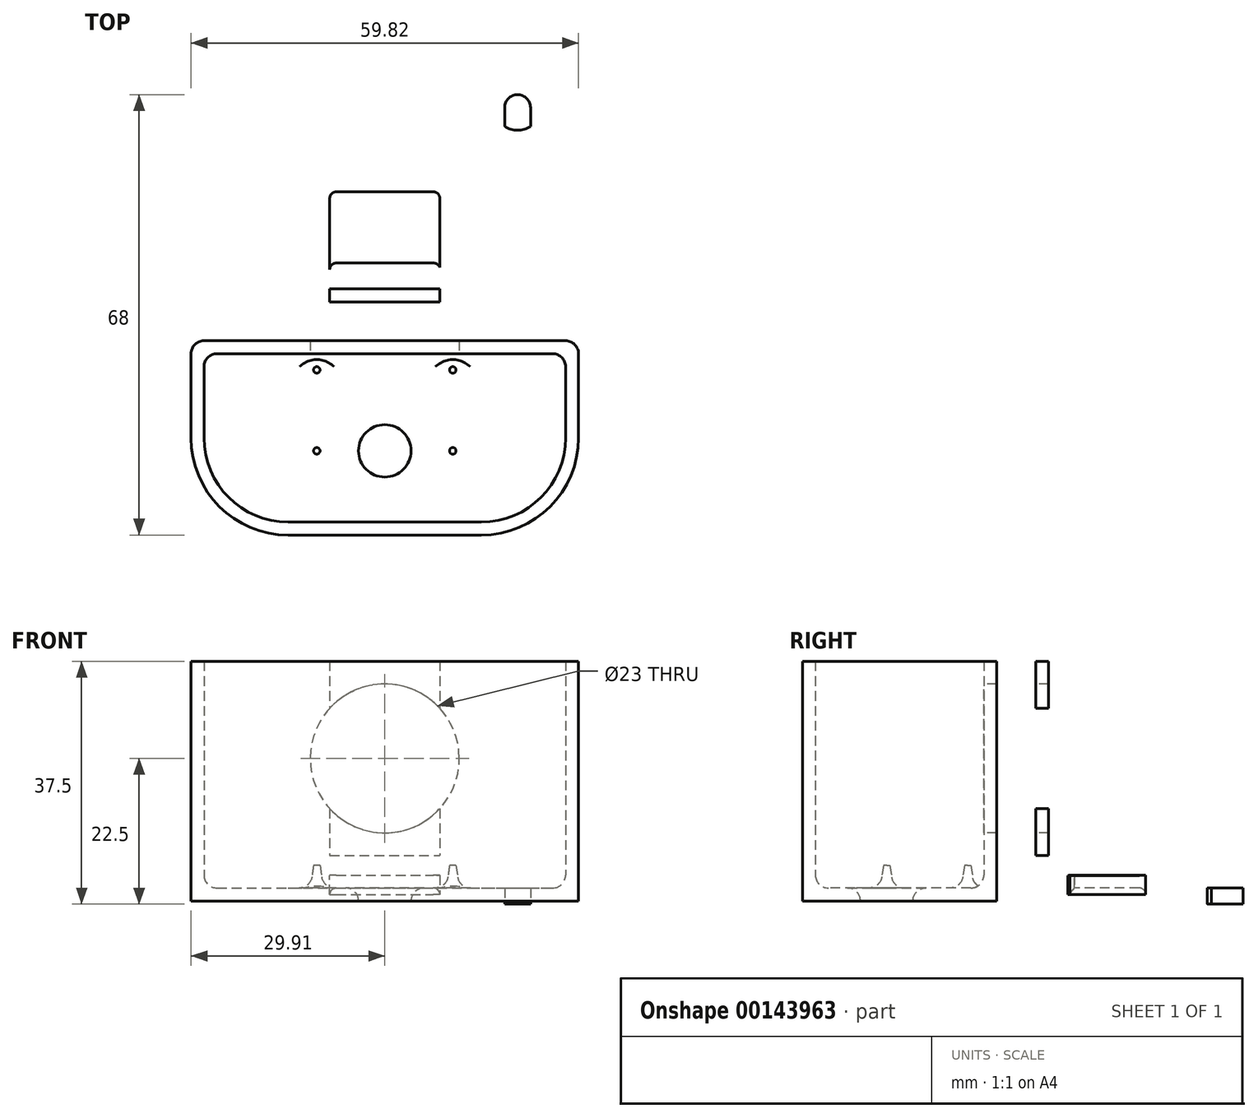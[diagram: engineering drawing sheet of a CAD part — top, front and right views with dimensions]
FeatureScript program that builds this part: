
annotation { "Feature Type Name" : "Feature", "Feature Type Description" : "" }
export const myFeature = defineFeature(function(context is Context, id is Id, definition is map)
    precondition{}
    {
        {
            var Q0;
            Q0=qCreatedBy(makeId("Top.planeOp"),FACE);
            var sketch = newSketch(context, id + "F0", { "sketchPlane" : qUnion([Q0])});
            skLineSegment(sketch, "E0", {"start": v(-28.5, 0) * mm, "end": v(-28.5, 42) * mm});
            skLineSegment(sketch, "E1", {"start": v(-26.5, 44) * mm, "end": v(26.5, 44) * mm});
            skLineSegment(sketch, "E2", {"start": v(28.5, 42) * mm, "end": v(28.5, 0) * mm});
            skLineSegment(sketch, "E3", {"start": v(28.5, 0) * mm, "end": v(28.5, -42) * mm});
            skLineSegment(sketch, "E4", {"start": v(26.5, -44) * mm, "end": v(-26.5, -44) * mm});
            skLineSegment(sketch, "E5", {"start": v(-28.5, -42) * mm, "end": v(-28.5, 0) * mm});
            skLineSegment(sketch, "E6", {"start": v(0, 0) * mm, "end": v(28.5, 0) * mm, "construction": true});
            skLineSegment(sketch, "E7", {"start": v(0, 0) * mm, "end": v(-28.5, 0) * mm, "construction": true});
            skPoint(sketch, "E8.visualSharp", {"position": v(-28.5, 44) * mm});
            skArc(sketch, "E8.filletArc", {"start": v(-26.5, 44) * mm, "mid": v(-27.91, 43.41) * mm, "end": v(-28.5, 42) * mm});
            skPoint(sketch, "E9.visualSharp", {"position": v(28.5, 44) * mm});
            skArc(sketch, "E9.filletArc", {"start": v(28.5, 42) * mm, "mid": v(27.91, 43.41) * mm, "end": v(26.5, 44) * mm});
            skPoint(sketch, "E10.visualSharp", {"position": v(28.5, -44) * mm});
            skArc(sketch, "E10.filletArc", {"start": v(26.5, -44) * mm, "mid": v(27.91, -43.41) * mm, "end": v(28.5, -42) * mm});
            skPoint(sketch, "E11.visualSharp", {"position": v(-28.5, -44) * mm});
            skArc(sketch, "E11.filletArc", {"start": v(-28.5, -42) * mm, "mid": v(-27.91, -43.41) * mm, "end": v(-26.5, -44) * mm});
            skLineSegment(sketch, "E12", {"start": v(-30.5, 0) * mm, "end": v(-30.5, 44) * mm});
            skLineSegment(sketch, "E13", {"start": v(-28.5, 46) * mm, "end": v(28.5, 46) * mm});
            skLineSegment(sketch, "E14", {"start": v(30.5, 44) * mm, "end": v(30.5, 0) * mm});
            skLineSegment(sketch, "E15", {"start": v(30.5, 0) * mm, "end": v(30.5, -44) * mm});
            skLineSegment(sketch, "E16", {"start": v(28.5, -46) * mm, "end": v(-28.5, -46) * mm});
            skLineSegment(sketch, "E17", {"start": v(-30.5, -44) * mm, "end": v(-30.5, 0) * mm});
            skPoint(sketch, "E18.visualSharp", {"position": v(-30.5, 46) * mm});
            skArc(sketch, "E18.filletArc", {"start": v(-28.5, 46) * mm, "mid": v(-29.91, 45.41) * mm, "end": v(-30.5, 44) * mm});
            skPoint(sketch, "E19.visualSharp", {"position": v(30.5, 46) * mm});
            skArc(sketch, "E19.filletArc", {"start": v(30.5, 44) * mm, "mid": v(29.91, 45.41) * mm, "end": v(28.5, 46) * mm});
            skPoint(sketch, "E20.visualSharp", {"position": v(30.5, -46) * mm});
            skArc(sketch, "E20.filletArc", {"start": v(28.5, -46) * mm, "mid": v(29.91, -45.41) * mm, "end": v(30.5, -44) * mm});
            skPoint(sketch, "E21.visualSharp", {"position": v(-30.5, -46) * mm});
            skArc(sketch, "E21.filletArc", {"start": v(-30.5, -44) * mm, "mid": v(-29.91, -45.41) * mm, "end": v(-28.5, -46) * mm});
            skLineSegment(sketch, "E22", {"start": v(0, 0) * mm, "end": v(0, -46) * mm, "construction": true});
            skLineSegment(sketch, "E23", {"start": v(10, -44) * mm, "end": v(10, -29) * mm});
            skLineSegment(sketch, "E24", {"start": v(-10, -29) * mm, "end": v(-10, -44) * mm});
            skLineSegment(sketch, "E25", {"start": v(-8, -27) * mm, "end": v(0, -27) * mm});
            skLineSegment(sketch, "E26", {"start": v(0, -27) * mm, "end": v(8, -27) * mm});
            skPoint(sketch, "E27.visualSharp", {"position": v(10, -27) * mm});
            skArc(sketch, "E27.filletArc", {"start": v(10, -29) * mm, "mid": v(9.41, -27.59) * mm, "end": v(8, -27) * mm});
            skPoint(sketch, "E28.visualSharp", {"position": v(-10, -27) * mm});
            skArc(sketch, "E28.filletArc", {"start": v(-8, -27) * mm, "mid": v(-9.41, -27.59) * mm, "end": v(-10, -29) * mm});
            skLineSegment(sketch, "E29", {"start": v(9.5, -44) * mm, "end": v(9.5, -41) * mm});
            skLineSegment(sketch, "E30", {"start": v(9.2, -40.7) * mm, "end": v(0, -40.7) * mm});
            skLineSegment(sketch, "E31", {"start": v(0, -40.7) * mm, "end": v(-5.2, -40.7) * mm});
            skLineSegment(sketch, "E32", {"start": v(-5.5, -41) * mm, "end": v(-5.5, -44) * mm});
            skPoint(sketch, "E33.visualSharp", {"position": v(9.5, -40.7) * mm});
            skArc(sketch, "E33.filletArc", {"start": v(9.5, -41) * mm, "mid": v(9.41, -40.79) * mm, "end": v(9.2, -40.7) * mm});
            skPoint(sketch, "E34.visualSharp", {"position": v(-5.5, -40.7) * mm});
            skArc(sketch, "E34.filletArc", {"start": v(-5.2, -40.7) * mm, "mid": v(-5.41, -40.79) * mm, "end": v(-5.5, -41) * mm});
            skLineSegment(sketch, "E35.bottom", {"start": v(-27.91, -52) * mm, "end": v(27.91, -52) * mm});
            skLineSegment(sketch, "E35.top", {"start": v(-14.91, -82) * mm, "end": v(14.91, -82) * mm});
            skLineSegment(sketch, "E35.left", {"start": v(-29.91, -54) * mm, "end": v(-29.91, -67) * mm});
            skLineSegment(sketch, "E35.right", {"start": v(29.91, -54) * mm, "end": v(29.91, -67) * mm});
            skPoint(sketch, "E35.middle", {"position": v(0, -67) * mm});
            skPoint(sketch, "E35.cornerSnap0", {"position": v(-29.91, -45.41) * mm});
            skLineSegment(sketch, "E36.bottom", {"start": v(-12.5, -54.5) * mm, "end": v(12.5, -54.5) * mm});
            skLineSegment(sketch, "E36.top", {"start": v(-12.5, -78.5) * mm, "end": v(12.5, -78.5) * mm});
            skLineSegment(sketch, "E36.left", {"start": v(-12.5, -54.5) * mm, "end": v(-12.5, -78.5) * mm});
            skLineSegment(sketch, "E36.right", {"start": v(12.5, -54.5) * mm, "end": v(12.5, -78.5) * mm});
            skLineSegment(sketch, "E37.bottom", {"start": v(-10.5, -56.5) * mm, "end": v(10.5, -56.5) * mm});
            skLineSegment(sketch, "E37.top", {"start": v(-10.5, -69) * mm, "end": v(10.5, -69) * mm});
            skLineSegment(sketch, "E37.left", {"start": v(-10.5, -56.5) * mm, "end": v(-10.5, -69) * mm});
            skLineSegment(sketch, "E37.right", {"start": v(10.5, -56.5) * mm, "end": v(10.5, -69) * mm});
            skPoint(sketch, "E38", {"position": v(0, -54.5) * mm});
            skLineSegment(sketch, "E39.bottom", {"start": v(-25.91, -54) * mm, "end": v(25.91, -54) * mm});
            skLineSegment(sketch, "E39.top", {"start": v(-14.91, -80) * mm, "end": v(14.91, -80) * mm});
            skLineSegment(sketch, "E39.left", {"start": v(-27.91, -56) * mm, "end": v(-27.91, -67) * mm});
            skLineSegment(sketch, "E39.right", {"start": v(27.91, -56) * mm, "end": v(27.91, -67) * mm});
            skCircle(sketch, "E40", {"center": v(-10.5, -56.5) * mm, "radius": 1 * mm});
            skCircle(sketch, "E41", {"center": v(10.5, -56.5) * mm, "radius": 1 * mm});
            skCircle(sketch, "E42", {"center": v(10.5, -69) * mm, "radius": 1 * mm});
            skCircle(sketch, "E43", {"center": v(-10.5, -69) * mm, "radius": 1 * mm});
            skCircle(sketch, "E44", {"center": v(0, -69) * mm, "radius": 4.05 * mm});
            skPoint(sketch, "E45.visualSharp", {"position": v(29.91, -52) * mm});
            skArc(sketch, "E45.filletArc", {"start": v(29.91, -54) * mm, "mid": v(29.33, -52.59) * mm, "end": v(27.91, -52) * mm});
            skArc(sketch, "E46.filletArc", {"start": v(27.91, -56) * mm, "mid": v(27.33, -54.59) * mm, "end": v(25.91, -54) * mm});
            skPoint(sketch, "E47.visualSharp", {"position": v(-27.91, -54) * mm});
            skArc(sketch, "E47.filletArc", {"start": v(-25.91, -54) * mm, "mid": v(-27.33, -54.59) * mm, "end": v(-27.91, -56) * mm});
            skPoint(sketch, "E48.visualSharp", {"position": v(-29.91, -52) * mm});
            skArc(sketch, "E48.filletArc", {"start": v(-27.91, -52) * mm, "mid": v(-29.33, -52.59) * mm, "end": v(-29.91, -54) * mm});
            skPoint(sketch, "E49.visualSharp", {"position": v(-27.91, -80) * mm});
            skArc(sketch, "E49.filletArc", {"start": v(-27.91, -67) * mm, "mid": v(-24.1, -76.2) * mm, "end": v(-14.91, -80) * mm});
            skPoint(sketch, "E50.visualSharp", {"position": v(-29.91, -82) * mm});
            skArc(sketch, "E50.filletArc", {"start": v(-29.91, -67) * mm, "mid": v(-25.52, -77.6) * mm, "end": v(-14.91, -82) * mm});
            skPoint(sketch, "E51.visualSharp", {"position": v(27.91, -80) * mm});
            skArc(sketch, "E51.filletArc", {"start": v(14.91, -80) * mm, "mid": v(24.1, -76.2) * mm, "end": v(27.91, -67) * mm});
            skPoint(sketch, "E52.visualSharp", {"position": v(29.91, -82) * mm});
            skArc(sketch, "E52.filletArc", {"start": v(14.91, -82) * mm, "mid": v(25.52, -77.6) * mm, "end": v(29.91, -67) * mm});
            skSolve(sketch);
        }
        {
            var Q0;
            Q0=makeQuery(id+"F0.imprint","IMPRINT",FACE,{"disambiguationData":[TD([[makeQuery(id+"F0.imprint","IMPRINT",EDGE,{"derivedFrom":sQuery(id+"F0.wireOp",EDGE,"E0")}),1.0]])]});
            extrude(context, id + "F1", {"entities" : qUnion([Q0]), "depth" : 35 * mm, "hasSecondDirection" : true, "secondDirectionOppositeDirection" : true, "secondDirectionDepth" : 2.5 * mm});
        }
        {
            var Q0;
            Q0=makeQuery(id+"F0.imprint","IMPRINT",FACE,{"disambiguationData":[TD([[makeQuery(id+"F0.imprint","IMPRINT",EDGE,{"derivedFrom":sQuery(id+"F0.wireOp",EDGE,"E0")}),-1.0]])]});
            extrude(context, id + "F2", {"entities" : qUnion([Q0]), "operationType" : NewBodyOperationType.ADD, "oppositeDirection" : true, "depth" : 2.5 * mm});
        }
        {
            var Q0;
            {var subQ2=sQuery(id+"F0.wireOp",EDGE,"E23");Q0=makeQuery(id+"F0.imprint","IMPRINT",FACE,{"disambiguationData":[TD([[makeQuery(id+"F0.imprint","IMPRINT",EDGE,{"derivedFrom":subQ2}),1.0]])]});}
            extrude(context, id + "F3", {"entities" : qUnion([Q0]), "operationType" : NewBodyOperationType.ADD, "depth" : 2 * mm, "hasSecondDirection" : true, "secondDirectionOppositeDirection" : true, "secondDirectionDepth" : 2.5 * mm});
        }
        {
            var Q0;
            Q0=makeQuery(id+"F3.opExtrude","CAP_EDGE",EDGE,{"disambiguationData":[OSD([sQuery(id+"F0.wireOp",EDGE,"E23")])],"isStart":false});
            fillet(context, id + "F4", {"entities" : qUnion([Q0]), "radius" : 2 * mm, "tangentPropagation" : true, "allowEdgeOverflow" : false});
        }
        {
            var Q0;
            Q0=makeQuery(id+"F1.opExtrude","SWEPT_FACE",FACE,{"disambiguationData":[OSD([sQuery(id+"F0.wireOp",EDGE,"E16")])]});
            var sketch = newSketch(context, id + "F5", { "sketchPlane" : qUnion([Q0])});
            skLineSegment(sketch, "E53.0", {"start": v(28.5, -2.5) * mm, "end": v(-28.5, -2.5) * mm});
            skLineSegment(sketch, "E54", {"start": v(-8.5, -2.5) * mm, "end": v(-8.5, 0) * mm});
            skLineSegment(sketch, "E55", {"start": v(-8.5, 0) * mm, "end": v(0, 0) * mm});
            skLineSegment(sketch, "E56", {"start": v(0, 0) * mm, "end": v(8.5, 0) * mm});
            skLineSegment(sketch, "E57", {"start": v(8.5, 0) * mm, "end": v(8.5, -2.5) * mm});
            skLineSegment(sketch, "E58", {"start": v(-8.5, 0) * mm, "end": v(-8.5, 5) * mm});
            skLineSegment(sketch, "E59", {"start": v(-8.5, 5) * mm, "end": v(8.5, 5) * mm});
            skLineSegment(sketch, "E60", {"start": v(8.5, 5) * mm, "end": v(8.5, 0) * mm});
            skSolve(sketch);
        }
        {
            var Q0;
            {var subQ0=sQuery(id+"F5.wireOp",EDGE,"E54");Q0=makeQuery(id+"F5.imprint","IMPRINT",FACE,{"disambiguationData":[TD([[makeQuery(id+"F5.imprint","IMPRINT",EDGE,{"derivedFrom":subQ0}),-1.0]])]});}
            extrude(context, id + "F6", {"entities" : qUnion([Q0]), "operationType" : NewBodyOperationType.REMOVE, "oppositeDirection" : true, "depth" : 17 * mm});
        }
        {
            var Q0;
            Q0=makeQuery(id+"F6.boolean.opBoolean","COPY",EDGE,{"derivedFrom":makeQuery(id+"F6.opExtrude","CAP_EDGE",EDGE,{"disambiguationData":[OSD([sQuery(id+"F5.wireOp",EDGE,"E54")])],"isStart":false})});
            var Q1;
            Q1=makeQuery(id+"F6.boolean.opBoolean","COPY",EDGE,{"derivedFrom":makeQuery(id+"F6.opExtrude","CAP_EDGE",EDGE,{"disambiguationData":[OSD([sQuery(id+"F5.wireOp",EDGE,"E57")])],"isStart":false})});
            fillet(context, id + "F7", {"entities" : qUnion([Q0, Q1]), "radius" : 1 * mm, "tangentPropagation" : true, "allowEdgeOverflow" : false});
        }
        {
            var Q0;
            Q0=makeQuery(id+"F5.imprint","IMPRINT",FACE,{"disambiguationData":[TD([[makeQuery(id+"F5.imprint","IMPRINT",EDGE,{"derivedFrom":sQuery(id+"F5.wireOp",EDGE,"E55")}),1.0]])]});
            extrude(context, id + "F8", {"entities" : qUnion([Q0]), "operationType" : NewBodyOperationType.REMOVE, "oppositeDirection" : true, "depth" : 6 * mm});
        }
        {
            var Q0;
            Q0=makeQuery(id+"F6.boolean.opBoolean","COPY",EDGE,{"derivedFrom":makeQuery(id+"F6.opExtrude","SWEPT_EDGE",EDGE,{"disambiguationData":[OSD([sQuery(id+"F5.wireOp",EDGE,"E54"),sQuery(id+"F5.wireOp",EDGE,"E55"),sQuery(id+"F5.wireOp",EDGE,"E58")])]})});
            var Q1;
            Q1=makeQuery(id+"F7.opFillet","BLEND_EDGE",EDGE,{"blendedFrom":[makeQuery(id+"F6.boolean.opBoolean","COPY",EDGE,{"derivedFrom":makeQuery(id+"F6.opExtrude","CAP_EDGE",EDGE,{"disambiguationData":[OSD([sQuery(id+"F5.wireOp",EDGE,"E54")])],"isStart":false})}),makeQuery(id+"F6.boolean.opBoolean","COPY",FACE,{"derivedFrom":makeQuery(id+"F6.opExtrude","SWEPT_FACE",FACE,{"disambiguationData":[OSD([sQuery(id+"F5.wireOp",EDGE,"E55"),sQuery(id+"F5.wireOp",EDGE,"E56")])]})})],"blendedInto":[makeQuery(id+"F6.boolean.opBoolean","COPY",FACE,{"derivedFrom":makeQuery(id+"F6.opExtrude","SWEPT_FACE",FACE,{"disambiguationData":[OSD([sQuery(id+"F5.wireOp",EDGE,"E55"),sQuery(id+"F5.wireOp",EDGE,"E56")])]})})]});
            var Q2;
            Q2=makeQuery(id+"F6.boolean.opBoolean","COPY",EDGE,{"derivedFrom":makeQuery(id+"F6.opExtrude","CAP_EDGE",EDGE,{"disambiguationData":[OSD([sQuery(id+"F5.wireOp",EDGE,"E55"),sQuery(id+"F5.wireOp",EDGE,"E56")])],"isStart":false})});
            var Q3;
            Q3=makeQuery(id+"F7.opFillet","BLEND_EDGE",EDGE,{"blendedFrom":[makeQuery(id+"F6.boolean.opBoolean","COPY",EDGE,{"derivedFrom":makeQuery(id+"F6.opExtrude","CAP_EDGE",EDGE,{"disambiguationData":[OSD([sQuery(id+"F5.wireOp",EDGE,"E57")])],"isStart":false})}),makeQuery(id+"F6.boolean.opBoolean","COPY",FACE,{"derivedFrom":makeQuery(id+"F6.opExtrude","SWEPT_FACE",FACE,{"disambiguationData":[OSD([sQuery(id+"F5.wireOp",EDGE,"E55"),sQuery(id+"F5.wireOp",EDGE,"E56")])]})})],"blendedInto":[makeQuery(id+"F6.boolean.opBoolean","COPY",FACE,{"derivedFrom":makeQuery(id+"F6.opExtrude","SWEPT_FACE",FACE,{"disambiguationData":[OSD([sQuery(id+"F5.wireOp",EDGE,"E55"),sQuery(id+"F5.wireOp",EDGE,"E56")])]})})]});
            var Q4;
            Q4=makeQuery(id+"F6.boolean.opBoolean","COPY",EDGE,{"derivedFrom":makeQuery(id+"F6.opExtrude","SWEPT_EDGE",EDGE,{"disambiguationData":[OSD([sQuery(id+"F5.wireOp",EDGE,"E56"),sQuery(id+"F5.wireOp",EDGE,"E57"),sQuery(id+"F5.wireOp",EDGE,"E60")])]})});
            fillet(context, id + "F9", {"entities" : qUnion([Q0, Q1, Q2, Q3, Q4]), "radius" : 1 * mm, "tangentPropagation" : true, "allowEdgeOverflow" : false});
        }
        {
            var Q0;
            Q0=makeQuery(id+"F8.boolean.opBoolean","COPY",EDGE,{"derivedFrom":makeQuery(id+"F8.opExtrude","CAP_EDGE",EDGE,{"disambiguationData":[OSD([sQuery(id+"F5.wireOp",EDGE,"E58")])],"isStart":false})});
            var Q1;
            Q1=makeQuery(id+"F8.boolean.opBoolean","COPY",EDGE,{"derivedFrom":makeQuery(id+"F8.opExtrude","CAP_EDGE",EDGE,{"disambiguationData":[OSD([sQuery(id+"F5.wireOp",EDGE,"E60")])],"isStart":false})});
            fillet(context, id + "F10", {"entities" : qUnion([Q0, Q1]), "radius" : 1 * mm, "tangentPropagation" : true, "allowEdgeOverflow" : false});
        }
        {
            var Q0;
            Q0=makeQuery(id+"F1.opExtrude","SWEPT_FACE",FACE,{"disambiguationData":[OSD([sQuery(id+"F0.wireOp",EDGE,"E13")])]});
            var sketch = newSketch(context, id + "F11", { "sketchPlane" : qUnion([Q0])});
            skLineSegment(sketch, "E61.0", {"start": v(-28.5, 35) * mm, "end": v(-28.5, -2.5) * mm});
            skLineSegment(sketch, "E62.0", {"start": v(28.5, -2.5) * mm, "end": v(-28.5, -2.5) * mm});
            skLineSegment(sketch, "E63.0", {"start": v(28.5, 35) * mm, "end": v(28.5, -2.5) * mm});
            skLineSegment(sketch, "E64", {"start": v(-30.5, 5) * mm, "end": v(30.5, 5) * mm, "construction": true});
            skLineSegment(sketch, "E65.0", {"start": v(30.5, 35) * mm, "end": v(30.5, -2.5) * mm});
            skLineSegment(sketch, "E66.0.0", {"start": v(-30.5, -2.5) * mm, "end": v(-28.5, -2.5) * mm});
            skLineSegment(sketch, "E66.0.1", {"start": v(-28.5, -2.5) * mm, "end": v(-28.5, 35) * mm});
            skLineSegment(sketch, "E66.0.2", {"start": v(-28.5, 35) * mm, "end": v(-30.5, 35) * mm});
            skLineSegment(sketch, "E66.0.3", {"start": v(-30.5, 35) * mm, "end": v(-30.5, -2.5) * mm});
            skLineSegment(sketch, "E67", {"start": v(-25.5, 5) * mm, "end": v(-9.5, 5) * mm});
            skLineSegment(sketch, "E68", {"start": v(-6, 5) * mm, "end": v(-6, 21) * mm});
            skLineSegment(sketch, "E69", {"start": v(-6, 21) * mm, "end": v(7.5, 21) * mm});
            skLineSegment(sketch, "E70", {"start": v(7.5, 21) * mm, "end": v(7.5, 5) * mm});
            skLineSegment(sketch, "E71", {"start": v(7.5, 5) * mm, "end": v(-6, 5) * mm});
            skLineSegment(sketch, "E72", {"start": v(12, 5) * mm, "end": v(12, 21) * mm});
            skLineSegment(sketch, "E73", {"start": v(12, 21) * mm, "end": v(25.5, 21) * mm});
            skLineSegment(sketch, "E74", {"start": v(25.5, 21) * mm, "end": v(25.5, 5) * mm});
            skLineSegment(sketch, "E75", {"start": v(25.5, 5) * mm, "end": v(12, 5) * mm});
            skPoint(sketch, "E76", {"position": v(-25.5, 5) * mm});
            skPoint(sketch, "E77", {"position": v(-9.5, 5) * mm});
            skLineSegment(sketch, "E78", {"start": v(-25.5, 5) * mm, "end": v(-25.5, 20.5) * mm});
            skLineSegment(sketch, "E79", {"start": v(-9.5, 5) * mm, "end": v(-9.5, 20.5) * mm});
            skLineSegment(sketch, "E80", {"start": v(-9.5, 20.5) * mm, "end": v(-25.5, 20.5) * mm});
            skSolve(sketch);
        }
        {
            var Q0;
            Q0=makeQuery(id+"F11.imprint","IMPRINT",FACE,{"disambiguationData":[TD([[makeQuery(id+"F11.imprint","IMPRINT",EDGE,{"derivedFrom":sQuery(id+"F11.wireOp",EDGE,"E67")}),1.0]])]});
            var Q1;
            Q1=makeQuery(id+"F11.imprint","IMPRINT",FACE,{"disambiguationData":[TD([[makeQuery(id+"F11.imprint","IMPRINT",EDGE,{"derivedFrom":sQuery(id+"F11.wireOp",EDGE,"E68")}),-1.0]])]});
            var Q2;
            Q2=makeQuery(id+"F11.imprint","IMPRINT",FACE,{"disambiguationData":[TD([[makeQuery(id+"F11.imprint","IMPRINT",EDGE,{"derivedFrom":sQuery(id+"F11.wireOp",EDGE,"E72")}),-1.0]])]});
            extrude(context, id + "F12", {"entities" : qUnion([Q0, Q1, Q2]), "operationType" : NewBodyOperationType.REMOVE, "endBound" : BoundingType.UP_TO_NEXT, "oppositeDirection" : true, "depth" : 25 * mm});
        }
        {
            var Q0;
            Q0=makeQuery(id+"F1.opExtrude","SWEPT_FACE",FACE,{"disambiguationData":[OSD([sQuery(id+"F0.wireOp",EDGE,"E14"),sQuery(id+"F0.wireOp",EDGE,"E15")])]});
            var sketch = newSketch(context, id + "F13", { "sketchPlane" : qUnion([Q0])});
            skLineSegment(sketch, "E81.0", {"start": v(-46, 35) * mm, "end": v(-46, -2.5) * mm});
            skLineSegment(sketch, "E81.1", {"start": v(-44, 35) * mm, "end": v(-44, -2.5) * mm});
            skLineSegment(sketch, "E81.2", {"start": v(44, 35) * mm, "end": v(44, -2.5) * mm});
            skLineSegment(sketch, "E81.3", {"start": v(46, 35) * mm, "end": v(46, -2.5) * mm});
            skLineSegment(sketch, "E81.4", {"start": v(44, -2.5) * mm, "end": v(-44, -2.5) * mm});
            skLineSegment(sketch, "E81.5", {"start": v(44, 35) * mm, "end": v(-44, 35) * mm});
            skLineSegment(sketch, "E81.6", {"start": v(-46, 35) * mm, "end": v(-44, 35) * mm});
            skLineSegment(sketch, "E81.7", {"start": v(-46, -2.5) * mm, "end": v(-44, -2.5) * mm});
            skLineSegment(sketch, "E81.8", {"start": v(44, -2.5) * mm, "end": v(46, -2.5) * mm});
            skLineSegment(sketch, "E81.9", {"start": v(44, 35) * mm, "end": v(46, 35) * mm});
            skCircle(sketch, "E82", {"center": v(9.5, 7.5) * mm, "radius": 3.5 * mm});
            skLineSegment(sketch, "E83", {"start": v(-20, 12.7) * mm, "end": v(-20, 4.7) * mm});
            skLineSegment(sketch, "E84", {"start": v(-20, 4.7) * mm, "end": v(-3, 4.7) * mm});
            skLineSegment(sketch, "E85", {"start": v(-3, 4.7) * mm, "end": v(-3, 12.7) * mm});
            skLineSegment(sketch, "E86", {"start": v(-3, 12.7) * mm, "end": v(-20, 12.7) * mm});
            skLineSegment(sketch, "E87.bottom", {"start": v(-37, 10.5) * mm, "end": v(-28, 10.5) * mm});
            skLineSegment(sketch, "E87.top", {"start": v(-37, 4.5) * mm, "end": v(-28, 4.5) * mm});
            skLineSegment(sketch, "E87.left", {"start": v(-37, 10.5) * mm, "end": v(-37, 4.5) * mm});
            skLineSegment(sketch, "E87.right", {"start": v(-28, 10.5) * mm, "end": v(-28, 4.5) * mm});
            skSolve(sketch);
        }
        {
            var Q0;
            Q0=makeQuery(id+"F13.imprint","IMPRINT",FACE,{"disambiguationData":[TD([[makeQuery(id+"F13.imprint","IMPRINT",EDGE,{"derivedFrom":sQuery(id+"F13.wireOp",EDGE,"E83")}),1.0]])]});
            var Q1;
            Q1=makeQuery(id+"F13.imprint","IMPRINT",FACE,{"disambiguationData":[TD([[makeQuery(id+"F13.imprint","IMPRINT",EDGE,{"derivedFrom":sQuery(id+"F13.wireOp",EDGE,"E82")}),1.0]])]});
            var Q2;
            Q2=makeQuery(id+"F13.imprint","IMPRINT",FACE,{"disambiguationData":[TD([[makeQuery(id+"F13.imprint","IMPRINT",EDGE,{"derivedFrom":sQuery(id+"F13.wireOp",EDGE,"E87.bottom")}),-1.0]])]});
            extrude(context, id + "F14", {"entities" : qUnion([Q0, Q1, Q2]), "operationType" : NewBodyOperationType.REMOVE, "endBound" : BoundingType.UP_TO_NEXT, "oppositeDirection" : true, "depth" : 25 * mm});
        }
        {
            var Q0;
            {var subQ0=sQuery(id+"F0.wireOp",EDGE,"E28.filletArc");var subQ1=sQuery(id+"F0.wireOp",EDGE,"E27.filletArc");var subQ2=sQuery(id+"F0.wireOp",EDGE,"E26");var subQ3=sQuery(id+"F0.wireOp",EDGE,"E25");var subQ4=sQuery(id+"F0.wireOp",EDGE,"E24");var subQ5=sQuery(id+"F0.wireOp",EDGE,"E23");var subQ6=sQuery(id+"F0.wireOp",EDGE,"E4");var subQ7=sQuery(id+"F0.wireOp",EDGE,"E11.filletArc");var subQ8=sQuery(id+"F0.wireOp",EDGE,"E10.filletArc");var subQ9=sQuery(id+"F0.wireOp",EDGE,"E9.filletArc");var subQ10=sQuery(id+"F0.wireOp",EDGE,"E8.filletArc");var subQ11=sQuery(id+"F0.wireOp",EDGE,"E5");var subQ12=sQuery(id+"F0.wireOp",EDGE,"E3");var subQ13=sQuery(id+"F0.wireOp",EDGE,"E2");var subQ14=sQuery(id+"F0.wireOp",EDGE,"E1");var subQ15=sQuery(id+"F0.wireOp",EDGE,"E0");Q0=makeQuery(id+"F3.boolean.opBoolean","MERGE",FACE,{"derivedFrom":[makeQuery(id+"F2.boolean.opBoolean","MERGE",FACE,{"derivedFrom":[makeQuery(id+"F1.opExtrude","CAP_FACE",FACE,{"disambiguationData":[OSD([subQ15,subQ14,subQ13,subQ12,subQ6,subQ11,subQ10,subQ9,subQ8,subQ7,sQuery(id+"F0.wireOp",EDGE,"E12"),sQuery(id+"F0.wireOp",EDGE,"E13"),sQuery(id+"F0.wireOp",EDGE,"E14"),sQuery(id+"F0.wireOp",EDGE,"E15"),sQuery(id+"F0.wireOp",EDGE,"E16"),sQuery(id+"F0.wireOp",EDGE,"E17"),sQuery(id+"F0.wireOp",EDGE,"E18.filletArc"),sQuery(id+"F0.wireOp",EDGE,"E19.filletArc"),sQuery(id+"F0.wireOp",EDGE,"E20.filletArc"),sQuery(id+"F0.wireOp",EDGE,"E21.filletArc")])],"isStart":true}),makeQuery(id+"F2.opExtrude","CAP_FACE",FACE,{"disambiguationData":[OSD([subQ15,subQ14,subQ13,subQ12,subQ6,subQ11,subQ10,subQ9,subQ8,subQ7,subQ5,subQ4,subQ3,subQ2,subQ1,subQ0])],"isStart":false})]}),makeQuery(id+"F3.opExtrude","CAP_FACE",FACE,{"disambiguationData":[OSD([subQ6,subQ5,subQ4,subQ3,subQ2,subQ1,subQ0,sQuery(id+"F0.wireOp",EDGE,"E29"),sQuery(id+"F0.wireOp",EDGE,"E30"),sQuery(id+"F0.wireOp",EDGE,"E31"),sQuery(id+"F0.wireOp",EDGE,"E32"),sQuery(id+"F0.wireOp",EDGE,"E33.filletArc"),sQuery(id+"F0.wireOp",EDGE,"E34.filletArc")])],"isStart":true})]});}
            var sketch = newSketch(context, id + "F15", { "sketchPlane" : qUnion([Q0])});
            skLineSegment(sketch, "E88", {"start": v(0, -46) * mm, "end": v(0, 45.82) * mm, "construction": true});
            skPoint(sketch, "E88.endSnap0", {"position": v(0, 29) * mm});
            skLineSegment(sketch, "E89.bottom", {"start": v(19.5, -33) * mm, "end": v(-19.5, -33) * mm});
            skLineSegment(sketch, "E89.top", {"start": v(19.5, -31) * mm, "end": v(-19.5, -31) * mm});
            skLineSegment(sketch, "E89.left", {"start": v(19.5, -33) * mm, "end": v(19.5, -31) * mm});
            skLineSegment(sketch, "E89.right", {"start": v(-19.5, -33) * mm, "end": v(-19.5, -31) * mm});
            skPoint(sketch, "E89.middle", {"position": v(0, -32) * mm});
            skLineSegment(sketch, "E90.0.1.0", {"start": v(19.5, -29.76) * mm, "end": v(-19.5, -29.76) * mm});
            skLineSegment(sketch, "E90.0.1.1", {"start": v(19.5, -29.76) * mm, "end": v(19.5, -27.76) * mm});
            skLineSegment(sketch, "E90.0.1.2", {"start": v(-19.5, -29.76) * mm, "end": v(-19.5, -27.76) * mm});
            skLineSegment(sketch, "E90.0.1.3", {"start": v(0, -42.76) * mm, "end": v(0, 49.06) * mm, "construction": true});
            skLineSegment(sketch, "E90.0.1.4", {"start": v(19.5, -27.76) * mm, "end": v(-19.5, -27.76) * mm});
            skLineSegment(sketch, "E90.0.2.0", {"start": v(19.5, -26.52) * mm, "end": v(-19.5, -26.52) * mm});
            skLineSegment(sketch, "E90.0.2.1", {"start": v(19.5, -26.52) * mm, "end": v(19.5, -24.52) * mm});
            skLineSegment(sketch, "E90.0.2.2", {"start": v(-19.5, -26.52) * mm, "end": v(-19.5, -24.52) * mm});
            skLineSegment(sketch, "E90.0.2.3", {"start": v(0, -39.52) * mm, "end": v(0, 52.3) * mm, "construction": true});
            skLineSegment(sketch, "E90.0.2.4", {"start": v(19.5, -24.52) * mm, "end": v(-19.5, -24.52) * mm});
            skLineSegment(sketch, "E90.0.3.0", {"start": v(19.5, -23.29) * mm, "end": v(-19.5, -23.29) * mm});
            skLineSegment(sketch, "E90.0.3.1", {"start": v(19.5, -23.29) * mm, "end": v(19.5, -21.29) * mm});
            skLineSegment(sketch, "E90.0.3.2", {"start": v(-19.5, -23.29) * mm, "end": v(-19.5, -21.29) * mm});
            skLineSegment(sketch, "E90.0.3.3", {"start": v(0, -36.29) * mm, "end": v(0, 55.54) * mm, "construction": true});
            skLineSegment(sketch, "E90.0.3.4", {"start": v(19.5, -21.29) * mm, "end": v(-19.5, -21.29) * mm});
            skLineSegment(sketch, "E90.0.4.0", {"start": v(19.5, -20.05) * mm, "end": v(-19.5, -20.05) * mm});
            skLineSegment(sketch, "E90.0.4.1", {"start": v(19.5, -20.05) * mm, "end": v(19.5, -18.05) * mm});
            skLineSegment(sketch, "E90.0.4.2", {"start": v(-19.5, -20.05) * mm, "end": v(-19.5, -18.05) * mm});
            skLineSegment(sketch, "E90.0.4.3", {"start": v(0, -33.05) * mm, "end": v(0, 58.78) * mm, "construction": true});
            skLineSegment(sketch, "E90.0.4.4", {"start": v(19.5, -18.05) * mm, "end": v(-19.5, -18.05) * mm});
            skLineSegment(sketch, "E90.0.5.0", {"start": v(19.5, -16.81) * mm, "end": v(-19.5, -16.81) * mm});
            skLineSegment(sketch, "E90.0.5.1", {"start": v(19.5, -16.81) * mm, "end": v(19.5, -14.81) * mm});
            skLineSegment(sketch, "E90.0.5.2", {"start": v(-19.5, -16.81) * mm, "end": v(-19.5, -14.81) * mm});
            skLineSegment(sketch, "E90.0.5.3", {"start": v(0, -29.81) * mm, "end": v(0, 62.01) * mm, "construction": true});
            skLineSegment(sketch, "E90.0.5.4", {"start": v(19.5, -14.81) * mm, "end": v(-19.5, -14.81) * mm});
            skLineSegment(sketch, "E90.0.6.0", {"start": v(19.5, -13.57) * mm, "end": v(-19.5, -13.57) * mm});
            skLineSegment(sketch, "E90.0.6.1", {"start": v(19.5, -13.57) * mm, "end": v(19.5, -11.57) * mm});
            skLineSegment(sketch, "E90.0.6.2", {"start": v(-19.5, -13.57) * mm, "end": v(-19.5, -11.57) * mm});
            skLineSegment(sketch, "E90.0.6.3", {"start": v(0, -26.57) * mm, "end": v(0, 65.25) * mm, "construction": true});
            skLineSegment(sketch, "E90.0.6.4", {"start": v(19.5, -11.57) * mm, "end": v(-19.5, -11.57) * mm});
            skLineSegment(sketch, "E90.0.7.0", {"start": v(19.5, -10.34) * mm, "end": v(-19.5, -10.34) * mm});
            skLineSegment(sketch, "E90.0.7.1", {"start": v(19.5, -10.34) * mm, "end": v(19.5, -8.34) * mm});
            skLineSegment(sketch, "E90.0.7.2", {"start": v(-19.5, -10.34) * mm, "end": v(-19.5, -8.34) * mm});
            skLineSegment(sketch, "E90.0.7.3", {"start": v(0, -23.34) * mm, "end": v(0, 68.49) * mm, "construction": true});
            skLineSegment(sketch, "E90.0.7.4", {"start": v(19.5, -8.34) * mm, "end": v(-19.5, -8.34) * mm});
            skLineSegment(sketch, "E90.0.8.0", {"start": v(19.5, -7.1) * mm, "end": v(-19.5, -7.1) * mm});
            skLineSegment(sketch, "E90.0.8.1", {"start": v(19.5, -7.1) * mm, "end": v(19.5, -5.1) * mm});
            skLineSegment(sketch, "E90.0.8.2", {"start": v(-19.5, -7.1) * mm, "end": v(-19.5, -5.1) * mm});
            skLineSegment(sketch, "E90.0.8.3", {"start": v(0, -20.1) * mm, "end": v(0, 71.73) * mm, "construction": true});
            skLineSegment(sketch, "E90.0.8.4", {"start": v(19.5, -5.1) * mm, "end": v(-19.5, -5.1) * mm});
            skLineSegment(sketch, "E90.0.9.0", {"start": v(19.5, -3.86) * mm, "end": v(-19.5, -3.86) * mm});
            skLineSegment(sketch, "E90.0.9.1", {"start": v(19.5, -3.86) * mm, "end": v(19.5, -1.86) * mm});
            skLineSegment(sketch, "E90.0.9.2", {"start": v(-19.5, -3.86) * mm, "end": v(-19.5, -1.86) * mm});
            skLineSegment(sketch, "E90.0.9.3", {"start": v(0, -16.86) * mm, "end": v(0, 74.96) * mm, "construction": true});
            skLineSegment(sketch, "E90.0.9.4", {"start": v(19.5, -1.86) * mm, "end": v(-19.5, -1.86) * mm});
            skLineSegment(sketch, "E90.direction1", {"start": v(-19.5, -33) * mm, "end": v(5.5, -33) * mm, "construction": true});
            skLineSegment(sketch, "E90.direction2", {"start": v(-19.5, -33) * mm, "end": v(-19.5, -29.76) * mm, "construction": true});
            skSolve(sketch);
        }
        {
            var Q0;
            Q0=makeQuery(id+"F15.imprint","IMPRINT",FACE,{"disambiguationData":[TD([[makeQuery(id+"F15.imprint","IMPRINT",EDGE,{"derivedFrom":sQuery(id+"F15.wireOp",EDGE,"E89.bottom")}),-1.0]])]});
            var Q1;
            Q1=makeQuery(id+"F15.imprint","IMPRINT",FACE,{"disambiguationData":[TD([[makeQuery(id+"F15.imprint","IMPRINT",EDGE,{"derivedFrom":sQuery(id+"F15.wireOp",EDGE,"E90.0.1.0")}),-1.0]])]});
            var Q2;
            Q2=makeQuery(id+"F15.imprint","IMPRINT",FACE,{"disambiguationData":[TD([[makeQuery(id+"F15.imprint","IMPRINT",EDGE,{"derivedFrom":sQuery(id+"F15.wireOp",EDGE,"E90.0.2.0")}),-1.0]])]});
            var Q3;
            Q3=makeQuery(id+"F15.imprint","IMPRINT",FACE,{"disambiguationData":[TD([[makeQuery(id+"F15.imprint","IMPRINT",EDGE,{"derivedFrom":sQuery(id+"F15.wireOp",EDGE,"E90.0.3.0")}),-1.0]])]});
            var Q4;
            Q4=makeQuery(id+"F15.imprint","IMPRINT",FACE,{"disambiguationData":[TD([[makeQuery(id+"F15.imprint","IMPRINT",EDGE,{"derivedFrom":sQuery(id+"F15.wireOp",EDGE,"E90.0.4.0")}),-1.0]])]});
            var Q5;
            Q5=makeQuery(id+"F15.imprint","IMPRINT",FACE,{"disambiguationData":[TD([[makeQuery(id+"F15.imprint","IMPRINT",EDGE,{"derivedFrom":sQuery(id+"F15.wireOp",EDGE,"E90.0.5.0")}),-1.0]])]});
            var Q6;
            Q6=makeQuery(id+"F15.imprint","IMPRINT",FACE,{"disambiguationData":[TD([[makeQuery(id+"F15.imprint","IMPRINT",EDGE,{"derivedFrom":sQuery(id+"F15.wireOp",EDGE,"E90.0.6.0")}),-1.0]])]});
            var Q7;
            Q7=makeQuery(id+"F15.imprint","IMPRINT",FACE,{"disambiguationData":[TD([[makeQuery(id+"F15.imprint","IMPRINT",EDGE,{"derivedFrom":sQuery(id+"F15.wireOp",EDGE,"E90.0.7.0")}),-1.0]])]});
            var Q8;
            Q8=makeQuery(id+"F15.imprint","IMPRINT",FACE,{"disambiguationData":[TD([[makeQuery(id+"F15.imprint","IMPRINT",EDGE,{"derivedFrom":sQuery(id+"F15.wireOp",EDGE,"E90.0.8.0")}),-1.0]])]});
            var Q9;
            Q9=makeQuery(id+"F15.imprint","IMPRINT",FACE,{"disambiguationData":[TD([[makeQuery(id+"F15.imprint","IMPRINT",EDGE,{"derivedFrom":sQuery(id+"F15.wireOp",EDGE,"E90.0.9.0")}),-1.0]])]});
            extrude(context, id + "F16", {"entities" : qUnion([Q0, Q1, Q2, Q3, Q4, Q5, Q6, Q7, Q8, Q9]), "operationType" : NewBodyOperationType.REMOVE, "endBound" : BoundingType.UP_TO_NEXT, "oppositeDirection" : true, "depth" : 25 * mm});
        }
        {
            var Q0;
            {var subQ0=sQuery(id+"F0.wireOp",EDGE,"E28.filletArc");var subQ1=sQuery(id+"F0.wireOp",EDGE,"E27.filletArc");var subQ2=sQuery(id+"F0.wireOp",EDGE,"E26");var subQ3=sQuery(id+"F0.wireOp",EDGE,"E25");var subQ4=sQuery(id+"F0.wireOp",EDGE,"E24");var subQ5=sQuery(id+"F0.wireOp",EDGE,"E23");var subQ6=sQuery(id+"F0.wireOp",EDGE,"E4");var subQ7=sQuery(id+"F0.wireOp",EDGE,"E11.filletArc");var subQ8=sQuery(id+"F0.wireOp",EDGE,"E10.filletArc");var subQ9=sQuery(id+"F0.wireOp",EDGE,"E9.filletArc");var subQ10=sQuery(id+"F0.wireOp",EDGE,"E8.filletArc");var subQ11=sQuery(id+"F0.wireOp",EDGE,"E5");var subQ12=sQuery(id+"F0.wireOp",EDGE,"E3");var subQ13=sQuery(id+"F0.wireOp",EDGE,"E2");var subQ14=sQuery(id+"F0.wireOp",EDGE,"E1");var subQ15=sQuery(id+"F0.wireOp",EDGE,"E0");Q0=makeQuery(id+"F3.boolean.opBoolean","MERGE",FACE,{"derivedFrom":[makeQuery(id+"F2.boolean.opBoolean","MERGE",FACE,{"derivedFrom":[makeQuery(id+"F1.opExtrude","CAP_FACE",FACE,{"disambiguationData":[OSD([subQ15,subQ14,subQ13,subQ12,subQ6,subQ11,subQ10,subQ9,subQ8,subQ7,sQuery(id+"F0.wireOp",EDGE,"E12"),sQuery(id+"F0.wireOp",EDGE,"E13"),sQuery(id+"F0.wireOp",EDGE,"E14"),sQuery(id+"F0.wireOp",EDGE,"E15"),sQuery(id+"F0.wireOp",EDGE,"E16"),sQuery(id+"F0.wireOp",EDGE,"E17"),sQuery(id+"F0.wireOp",EDGE,"E18.filletArc"),sQuery(id+"F0.wireOp",EDGE,"E19.filletArc"),sQuery(id+"F0.wireOp",EDGE,"E20.filletArc"),sQuery(id+"F0.wireOp",EDGE,"E21.filletArc")])],"isStart":true}),makeQuery(id+"F2.opExtrude","CAP_FACE",FACE,{"disambiguationData":[OSD([subQ15,subQ14,subQ13,subQ12,subQ6,subQ11,subQ10,subQ9,subQ8,subQ7,subQ5,subQ4,subQ3,subQ2,subQ1,subQ0])],"isStart":false})]}),makeQuery(id+"F3.opExtrude","CAP_FACE",FACE,{"disambiguationData":[OSD([subQ6,subQ5,subQ4,subQ3,subQ2,subQ1,subQ0,sQuery(id+"F0.wireOp",EDGE,"E29"),sQuery(id+"F0.wireOp",EDGE,"E30"),sQuery(id+"F0.wireOp",EDGE,"E31"),sQuery(id+"F0.wireOp",EDGE,"E32"),sQuery(id+"F0.wireOp",EDGE,"E33.filletArc"),sQuery(id+"F0.wireOp",EDGE,"E34.filletArc")])],"isStart":true})]});}
            var sketch = newSketch(context, id + "F17", { "sketchPlane" : qUnion([Q0])});
            skLineSegment(sketch, "E91", {"start": v(0, 0) * mm, "end": v(0, 16) * mm, "construction": true});
            skLineSegment(sketch, "E92", {"start": v(-20.5, 16) * mm, "end": v(17.1, 16) * mm, "construction": true});
            skCircle(sketch, "E93", {"center": v(-20.5, 16) * mm, "radius": 3.5 * mm});
            skCircle(sketch, "E94", {"center": v(-20.5, 16) * mm, "radius": 2 * mm});
            skCircle(sketch, "E95.MirrorC", {"center": v(20.5, 16) * mm, "radius": 3.5 * mm});
            skCircle(sketch, "E96.MirrorC", {"center": v(20.5, 16) * mm, "radius": 2 * mm});
            skLineSegment(sketch, "E97.MirrorCS", {"start": v(-18.5, 24.4) * mm, "end": v(-18.5, 16) * mm});
            skLineSegment(sketch, "E98.MirrorCS", {"start": v(-22.5, 16) * mm, "end": v(-22.5, 24.4) * mm});
            skLineSegment(sketch, "E99.MirrorCS", {"start": v(-21.9, 25) * mm, "end": v(-19.1, 25) * mm});
            skArc(sketch, "E100.MirrorCS", {"start": v(-19.1, 25) * mm, "mid": v(-18.68, 24.82) * mm, "end": v(-18.5, 24.4) * mm});
            skArc(sketch, "E101.MirrorCS", {"start": v(-22.5, 24.4) * mm, "mid": v(-22.32, 24.82) * mm, "end": v(-21.9, 25) * mm});
            skLineSegment(sketch, "E102.MirrorCS", {"start": v(18.5, 24.4) * mm, "end": v(18.5, 16) * mm});
            skLineSegment(sketch, "E103.MirrorCS", {"start": v(22.5, 16) * mm, "end": v(22.5, 24.4) * mm});
            skLineSegment(sketch, "E104.MirrorCS", {"start": v(21.9, 25) * mm, "end": v(19.1, 25) * mm});
            skArc(sketch, "E105.MirrorCS", {"start": v(22.5, 24.4) * mm, "mid": v(22.32, 24.82) * mm, "end": v(21.9, 25) * mm});
            skArc(sketch, "E106.MirrorCS", {"start": v(19.1, 25) * mm, "mid": v(18.68, 24.82) * mm, "end": v(18.5, 24.4) * mm});
            skSolve(sketch);
        }
        {
            var Q0;
            {var subQ0=sQuery(id+"F17.wireOp",EDGE,"E102.MirrorCS");var subQ1=sQuery(id+"F17.wireOp",EDGE,"E95.MirrorC");var subQ2=makeQuery(id+"F17.imprint","INTERSECT",VERTEX,{"derivedFrom":[subQ1,subQ0]});Q0=makeQuery(id+"F17.imprint","IMPRINT",FACE,{"disambiguationData":[TD([[makeQuery(id+"F17.imprint","IMPRINT",EDGE,{"disambiguationData":[TD([[subQ2,1.0]])],"derivedFrom":subQ1}),-1.0]])]});}
            var Q1;
            {var subQ0=sQuery(id+"F17.wireOp",EDGE,"E96.MirrorC");var subQ1=makeQuery(id+"F17.imprint","INTERSECT",VERTEX,{"derivedFrom":[subQ0,sQuery(id+"F17.wireOp",EDGE,"E102.MirrorCS")]});Q1=makeQuery(id+"F17.imprint","IMPRINT",FACE,{"disambiguationData":[TD([[makeQuery(id+"F17.imprint","IMPRINT",EDGE,{"disambiguationData":[TD([[subQ1,-1.0]])],"derivedFrom":subQ0}),-1.0]])]});}
            var Q2;
            Q2=makeQuery(id+"F17.imprint","IMPRINT",FACE,{"disambiguationData":[TD([[makeQuery(id+"F17.imprint","IMPRINT",EDGE,{"derivedFrom":sQuery(id+"F17.wireOp",EDGE,"E104.MirrorCS")}),1.0]])]});
            var Q3;
            {var subQ0=sQuery(id+"F17.wireOp",EDGE,"E97.MirrorCS");var subQ1=sQuery(id+"F17.wireOp",EDGE,"E93");var subQ2=makeQuery(id+"F17.imprint","INTERSECT",VERTEX,{"derivedFrom":[subQ1,subQ0]});Q3=makeQuery(id+"F17.imprint","IMPRINT",FACE,{"disambiguationData":[TD([[makeQuery(id+"F17.imprint","IMPRINT",EDGE,{"disambiguationData":[TD([[subQ2,1.0]])],"derivedFrom":subQ1}),1.0]])]});}
            var Q4;
            {var subQ0=sQuery(id+"F17.wireOp",EDGE,"E97.MirrorCS");var subQ1=sQuery(id+"F17.wireOp",EDGE,"E93");var subQ2=makeQuery(id+"F17.imprint","INTERSECT",VERTEX,{"derivedFrom":[subQ1,subQ0]});Q4=makeQuery(id+"F17.imprint","IMPRINT",FACE,{"disambiguationData":[TD([[makeQuery(id+"F17.imprint","IMPRINT",EDGE,{"disambiguationData":[TD([[subQ2,-1.0]])],"derivedFrom":subQ1}),1.0]])]});}
            var Q5;
            Q5=makeQuery(id+"F17.imprint","IMPRINT",FACE,{"disambiguationData":[TD([[makeQuery(id+"F17.imprint","IMPRINT",EDGE,{"derivedFrom":sQuery(id+"F17.wireOp",EDGE,"E99.MirrorCS")}),-1.0]])]});
            var Q6;
            {var subQ0=sQuery(id+"F17.wireOp",EDGE,"E94");var subQ1=makeQuery(id+"F17.imprint","INTERSECT",VERTEX,{"derivedFrom":[subQ0,sQuery(id+"F17.wireOp",EDGE,"E97.MirrorCS")]});Q6=makeQuery(id+"F17.imprint","IMPRINT",FACE,{"disambiguationData":[TD([[makeQuery(id+"F17.imprint","IMPRINT",EDGE,{"disambiguationData":[TD([[subQ1,-1.0]])],"derivedFrom":subQ0}),1.0]])]});}
            var Q7;
            {var subQ0=sQuery(id+"F17.wireOp",EDGE,"E102.MirrorCS");var subQ1=sQuery(id+"F17.wireOp",EDGE,"E95.MirrorC");var subQ2=makeQuery(id+"F17.imprint","INTERSECT",VERTEX,{"derivedFrom":[subQ1,subQ0]});Q7=makeQuery(id+"F17.imprint","IMPRINT",FACE,{"disambiguationData":[TD([[makeQuery(id+"F17.imprint","IMPRINT",EDGE,{"disambiguationData":[TD([[subQ2,-1.0]])],"derivedFrom":subQ1}),-1.0]])]});}
            extrude(context, id + "F18", {"entities" : qUnion([Q0, Q1, Q2, Q3, Q4, Q5, Q6, Q7]), "operationType" : NewBodyOperationType.REMOVE, "endBound" : BoundingType.UP_TO_NEXT, "oppositeDirection" : true, "depth" : 25 * mm});
        }
        {
            var Q0;
            {var subQ0=sQuery(id+"F5.wireOp",EDGE,"E54");Q0=makeQuery(id+"F5.imprint","IMPRINT",FACE,{"disambiguationData":[TD([[makeQuery(id+"F5.imprint","IMPRINT",EDGE,{"derivedFrom":subQ0}),1.0]])]});}
            var sketch = newSketch(context, id + "F19", { "sketchPlane" : qUnion([Q0])});
            skLineSegment(sketch, "E107.0", {"start": v(-28.5, 35) * mm, "end": v(-28.5, -2.5) * mm});
            skLineSegment(sketch, "E107.1", {"start": v(28.5, 35) * mm, "end": v(28.5, -2.5) * mm});
            skCircle(sketch, "E108", {"center": v(0, 20) * mm, "radius": 11.5 * mm});
            skLineSegment(sketch, "E109.0", {"start": v(-8.5, 5) * mm, "end": v(8.5, 5) * mm});
            skLineSegment(sketch, "E110", {"start": v(28.5, 5) * mm, "end": v(-28.5, 5) * mm, "construction": true});
            skLineSegment(sketch, "E111", {"start": v(-28.5, 5) * mm, "end": v(28.5, 35) * mm, "construction": true});
            skLineSegment(sketch, "E112", {"start": v(28.5, 5) * mm, "end": v(-28.5, 35) * mm, "construction": true});
            skSolve(sketch);
        }
        {
            var Q0;
            Q0=makeQuery(id+"F19.imprint","IMPRINT",FACE,{"disambiguationData":[TD([[makeQuery(id+"F19.imprint","IMPRINT",EDGE,{"derivedFrom":sQuery(id+"F19.wireOp",EDGE,"E108")}),1.0]])]});
            extrude(context, id + "F20", {"entities" : qUnion([Q0]), "operationType" : NewBodyOperationType.REMOVE, "endBound" : BoundingType.UP_TO_NEXT, "oppositeDirection" : true, "depth" : 25 * mm});
        }
        {
            var Q0;
            Q0=qCreatedBy(makeId("Top.planeOp"),FACE);
            var sketch = newSketch(context, id + "F21", { "sketchPlane" : qUnion([Q0])});
            skLineSegment(sketch, "E113.0", {"start": v(-29.91, -54) * mm, "end": v(-29.91, -67) * mm});
            skLineSegment(sketch, "E114.0", {"start": v(-27.91, -52) * mm, "end": v(27.91, -52) * mm});
            skLineSegment(sketch, "E115.0", {"start": v(29.91, -54) * mm, "end": v(29.91, -67) * mm});
            skLineSegment(sketch, "E116.0", {"start": v(-14.91, -82) * mm, "end": v(14.91, -82) * mm});
            skArc(sketch, "E117.0", {"start": v(-29.91, -67) * mm, "mid": v(-25.52, -77.6) * mm, "end": v(-14.91, -82) * mm});
            skArc(sketch, "E118.0", {"start": v(14.91, -82) * mm, "mid": v(25.52, -77.6) * mm, "end": v(29.91, -67) * mm});
            skArc(sketch, "E119.0", {"start": v(-27.91, -52) * mm, "mid": v(-29.33, -52.59) * mm, "end": v(-29.91, -54) * mm});
            skArc(sketch, "E120.0", {"start": v(29.91, -54) * mm, "mid": v(29.33, -52.59) * mm, "end": v(27.91, -52) * mm});
            skSolve(sketch);
        }
        {
            var Q0;
            Q0=makeQuery(id+"F21.imprint","IMPRINT",FACE,{"disambiguationData":[TD([[makeQuery(id+"F21.imprint","IMPRINT",EDGE,{"derivedFrom":sQuery(id+"F21.wireOp",EDGE,"E113.0")}),1.0]])]});
            extrude(context, id + "F22", {"entities" : qUnion([Q0]), "oppositeDirection" : true, "depth" : 2 * mm});
        }
        {
            var Q0;
            Q0=makeQuery(id+"F0.imprint","IMPRINT",FACE,{"disambiguationData":[TD([[makeQuery(id+"F0.imprint","IMPRINT",EDGE,{"derivedFrom":sQuery(id+"F0.wireOp",EDGE,"E35.bottom")}),-1.0]])]});
            extrude(context, id + "F23", {"entities" : qUnion([Q0]), "operationType" : NewBodyOperationType.ADD, "depth" : 35 * mm});
        }
        {
            var Q0;
            Q0=makeQuery(id+"F23.opExtrude","SWEPT_FACE",FACE,{"disambiguationData":[OSD([sQuery(id+"F0.wireOp",EDGE,"E39.bottom")])]});
            var sketch = newSketch(context, id + "F24", { "sketchPlane" : qUnion([Q0])});
            skCircle(sketch, "E121.0", {"center": v(0, 20) * mm, "radius": 11.5 * mm});
            skSolve(sketch);
        }
        {
            var Q0;
            Q0=makeQuery(id+"F24.imprint","IMPRINT",FACE,{"disambiguationData":[TD([[makeQuery(id+"F24.imprint","IMPRINT",EDGE,{"derivedFrom":sQuery(id+"F24.wireOp",EDGE,"E121.0")}),1.0]])]});
            extrude(context, id + "F25", {"entities" : qUnion([Q0]), "operationType" : NewBodyOperationType.REMOVE, "endBound" : BoundingType.UP_TO_NEXT, "oppositeDirection" : true, "depth" : 25 * mm});
        }
        {
            var Q0;
            Q0=makeQuery(id+"F0.imprint","IMPRINT",FACE,{"disambiguationData":[TD([[makeQuery(id+"F0.imprint","IMPRINT",EDGE,{"derivedFrom":sQuery(id+"F0.wireOp",EDGE,"E36.bottom")}),1.0]])]});
            cPlane(context, id + "F26", {"entities" : qUnion([Q0]), "cplaneType" : CPlaneType.OFFSET, "offset" : 3.5 * mm, "width" : 150 * mm, "height" : 150 * mm});
        }
        {
            var Q0;
            Q0=qCreatedBy(id+"F26.planeOp",FACE);
            var sketch = newSketch(context, id + "F27", { "sketchPlane" : qUnion([Q0])});
            skCircle(sketch, "E122.0", {"center": v(10.5, -56.5) * mm, "radius": 1 * mm});
            skCircle(sketch, "E123.0", {"center": v(10.5, -69) * mm, "radius": 1 * mm});
            skCircle(sketch, "E124.0", {"center": v(-10.5, -56.5) * mm, "radius": 1 * mm});
            skCircle(sketch, "E125.0", {"center": v(-10.5, -69) * mm, "radius": 1 * mm});
            skCircle(sketch, "E126", {"center": v(10.5, -56.5) * mm, "radius": 0.5 * mm});
            skCircle(sketch, "E127", {"center": v(10.5, -69) * mm, "radius": 0.5 * mm});
            skCircle(sketch, "E128", {"center": v(-10.5, -69) * mm, "radius": 0.5 * mm});
            skCircle(sketch, "E129", {"center": v(-10.5, -56.5) * mm, "radius": 0.5 * mm});
            skSolve(sketch);
        }
        {
            var Q0;
            Q0=makeQuery(id+"F0.imprint","IMPRINT",FACE,{"disambiguationData":[TD([[makeQuery(id+"F0.imprint","IMPRINT",EDGE,{"derivedFrom":sQuery(id+"F0.wireOp",EDGE,"E36.bottom")}),1.0]])]});
            var sketch = newSketch(context, id + "F28", { "sketchPlane" : qUnion([Q0])});
            skCircle(sketch, "E130.0", {"center": v(10.5, -56.5) * mm, "radius": 1 * mm});
            skCircle(sketch, "E131.0", {"center": v(10.5, -69) * mm, "radius": 1 * mm});
            skCircle(sketch, "E132.0", {"center": v(-10.5, -56.5) * mm, "radius": 1 * mm});
            skCircle(sketch, "E133.0", {"center": v(-10.5, -69) * mm, "radius": 1 * mm});
            skSolve(sketch);
        }
        {
            var Q1;
            Q1=makeQuery(id+"F28.imprint","IMPRINT",FACE,{"disambiguationData":[TD([[makeQuery(id+"F28.imprint","IMPRINT",EDGE,{"derivedFrom":sQuery(id+"F28.wireOp",EDGE,"E132.0")}),1.0]])]});
            var Q2;
            Q2=makeQuery(id+"F27.imprint","IMPRINT",FACE,{"disambiguationData":[TD([[makeQuery(id+"F27.imprint","IMPRINT",EDGE,{"derivedFrom":sQuery(id+"F27.wireOp",EDGE,"E129")}),1.0]])]});
            loft(context, id + "F29", {"operationType" : NewBodyOperationType.ADD, "sheetProfilesArray" : [{ "sheetProfileEntities" : qUnion([Q1]) }, { "sheetProfileEntities" : qUnion([Q2]) }]});
        }
        {
            var Q1;
            Q1=makeQuery(id+"F28.imprint","IMPRINT",FACE,{"disambiguationData":[TD([[makeQuery(id+"F28.imprint","IMPRINT",EDGE,{"derivedFrom":sQuery(id+"F28.wireOp",EDGE,"E133.0")}),1.0]])]});
            var Q2;
            Q2=makeQuery(id+"F27.imprint","IMPRINT",FACE,{"disambiguationData":[TD([[makeQuery(id+"F27.imprint","IMPRINT",EDGE,{"derivedFrom":sQuery(id+"F27.wireOp",EDGE,"E128")}),1.0]])]});
            loft(context, id + "F30", {"operationType" : NewBodyOperationType.ADD, "sheetProfilesArray" : [{ "sheetProfileEntities" : qUnion([Q1]) }, { "sheetProfileEntities" : qUnion([Q2]) }]});
        }
        {
            var Q1;
            Q1=makeQuery(id+"F28.imprint","IMPRINT",FACE,{"disambiguationData":[TD([[makeQuery(id+"F28.imprint","IMPRINT",EDGE,{"derivedFrom":sQuery(id+"F28.wireOp",EDGE,"E131.0")}),1.0]])]});
            var Q2;
            Q2=makeQuery(id+"F27.imprint","IMPRINT",FACE,{"disambiguationData":[TD([[makeQuery(id+"F27.imprint","IMPRINT",EDGE,{"derivedFrom":sQuery(id+"F27.wireOp",EDGE,"E127")}),1.0]])]});
            loft(context, id + "F31", {"operationType" : NewBodyOperationType.ADD, "sheetProfilesArray" : [{ "sheetProfileEntities" : qUnion([Q1]) }, { "sheetProfileEntities" : qUnion([Q2]) }]});
        }
        {
            var Q1;
            Q1=makeQuery(id+"F27.imprint","IMPRINT",FACE,{"disambiguationData":[TD([[makeQuery(id+"F27.imprint","IMPRINT",EDGE,{"derivedFrom":sQuery(id+"F27.wireOp",EDGE,"E126")}),1.0]])]});
            var Q2;
            Q2=makeQuery(id+"F28.imprint","IMPRINT",FACE,{"disambiguationData":[TD([[makeQuery(id+"F28.imprint","IMPRINT",EDGE,{"derivedFrom":sQuery(id+"F28.wireOp",EDGE,"E130.0")}),1.0]])]});
            loft(context, id + "F32", {"operationType" : NewBodyOperationType.ADD, "sheetProfilesArray" : [{ "sheetProfileEntities" : qUnion([Q1]) }, { "sheetProfileEntities" : qUnion([Q2]) }]});
        }
        {
            var Q0;
            {var subQ0=sQuery(id+"F0.wireOp",EDGE,"E44");var subQ1=sQuery(id+"F0.wireOp",EDGE,"E37.top");var subQ2=makeQuery(id+"F0.imprint","INTERSECT",VERTEX,{"disambiguationData":[OD(0.0)],"derivedFrom":[subQ1,subQ0]});Q0=makeQuery(id+"F0.imprint","IMPRINT",FACE,{"disambiguationData":[TD([[makeQuery(id+"F0.imprint","IMPRINT",EDGE,{"disambiguationData":[TD([[subQ2,-1.0]])],"derivedFrom":subQ1}),-1.0]])]});}
            var Q1;
            {var subQ0=sQuery(id+"F0.wireOp",EDGE,"E44");var subQ1=sQuery(id+"F0.wireOp",EDGE,"E37.top");var subQ2=makeQuery(id+"F0.imprint","INTERSECT",VERTEX,{"disambiguationData":[OD(0.0)],"derivedFrom":[subQ1,subQ0]});Q1=makeQuery(id+"F0.imprint","IMPRINT",FACE,{"disambiguationData":[TD([[makeQuery(id+"F0.imprint","IMPRINT",EDGE,{"disambiguationData":[TD([[subQ2,-1.0]])],"derivedFrom":subQ1}),1.0]])]});}
            extrude(context, id + "F33", {"entities" : qUnion([Q0, Q1]), "operationType" : NewBodyOperationType.REMOVE, "endBound" : BoundingType.UP_TO_NEXT, "oppositeDirection" : true, "depth" : 25 * mm});
        }
        {
            var Q0;
            Q0=makeQuery(id+"F22.opExtrude","CAP_FACE",FACE,{"disambiguationData":[OSD([sQuery(id+"F21.wireOp",EDGE,"E113.0"),sQuery(id+"F21.wireOp",EDGE,"E114.0"),sQuery(id+"F21.wireOp",EDGE,"E115.0"),sQuery(id+"F21.wireOp",EDGE,"E116.0"),sQuery(id+"F21.wireOp",EDGE,"E117.0"),sQuery(id+"F21.wireOp",EDGE,"E118.0"),sQuery(id+"F21.wireOp",EDGE,"E119.0"),sQuery(id+"F21.wireOp",EDGE,"E120.0")])],"isStart":true});
            fillet(context, id + "F34", {"entities" : qUnion([Q0]), "radius" : 2 * mm, "tangentPropagation" : true, "allowEdgeOverflow" : false});
        }
    });
